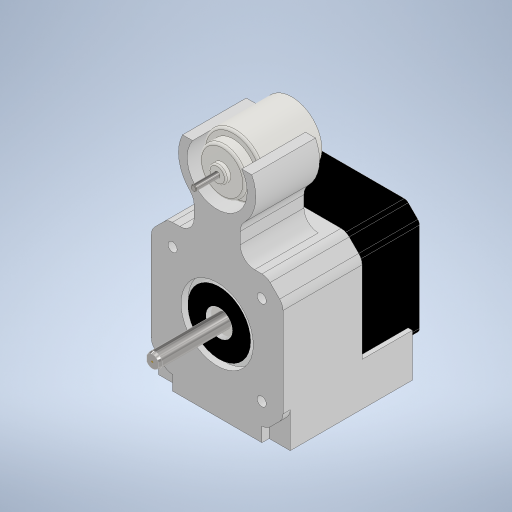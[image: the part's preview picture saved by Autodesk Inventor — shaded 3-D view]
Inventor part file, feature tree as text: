
AUTODESK INVENTOR PART (.ipt)
format: ipt  version: 2024.1 (Build 281209000, 209)  size: 689,664 bytes
history: native  units: mm
features: sketch x23, extrude x21, projected_geometry x11, fillet x10, other x5, chamfer x3
ambient origin geometry x8: Origin, YZ Plane, XZ Plane, XY Plane, X Axis, Y Axis, Z Axis, Center Point
bodies: Solid7 (feature_tree)
feature tree (73):
  other  "stepper"
  extrude  "Extrusion1"  Depth=41.8mm
  chamfer  "Chamfer1"  Distance=47.0mm
  fillet  "Fillet1"  Radius=2.0mm
  extrude  "Extrusion2"  Depth=41.8mm
  extrude  "Extrusion3"  Depth=20.9mm
  chamfer  "Chamfer2"  Distance=1.79mm
  other  "Work Point1"
  extrude  "Extrusion4"  Depth=5.0mm
  fillet  "Fillet2"  Radius=25.0mm
  extrude  "Extrusion5"  Depth=2.0mm
  extrude  "Extrusion6"  Depth=1.0mm
  extrude  "Extrusion7"  Depth=5.4mm
  extrude  "Extrusion8"  Depth=31.0mm
  extrude  "Extrusion9"  Depth=3.2mm
  extrude  "Extrusion16"  Depth=2.0mm
  fillet  "Fillet6"  Radius=2.5mm
  extrude  "Extrusion17"  Depth=42.5mm TaperAngle=0.0deg
  extrude  "Extrusion18"  Depth=5.0mm
  fillet  "Fillet7"  Radius=25.0mm
  fillet  "Fillet8"  Radius=20.9mm
  extrude  "Extrusion19"  Depth=45.8mm
  fillet  "Fillet9"  Radius=21.0mm
  extrude  "Extrusion20"  Depth=16.0mm
  fillet  "Fillet10"  Radius=3.8mm
  extrude  "Extrusion21"  Depth=6.05mm
  extrude  "Extrusion10"  Depth=2.0mm
  sketch  "Sketch11"  dims[d30=5.4mm d31=3.2mm]
  fillet  "Fillet3"  Radius=8.56mm
  extrude  "Extrusion11"  Depth=2.0mm
  fillet  "Fillet4"  Radius=18.75mm
  extrude  "Extrusion12"  Depth=5.0mm TaperAngle=45.0deg
  extrude  "Extrusion13"  Depth=33.35mm
  fillet  "Fillet5"  Radius=33.35mm
  extrude  "Extrusion14"  Depth=1.96mm
  extrude  "Extrusion15"  Depth=5.0mm
  chamfer  "Chamfer3"  Distance=6.03mm
  sketch  "Sketch17"  dims[d54=1.25mm d55=6.05mm]
  sketch  "Sketch1"  dims[d0=41.8mm d1=41.8mm d2=47.0mm d3=0.0mm]
  sketch  "Sketch2"  dims[d4=4.5mm d5=2.0mm d6=45.0deg d7=2.0mm]
  sketch  "Sketch3"  dims[d8=22.0mm d9=41.8mm]
  sketch  "Sketch4"  dims[d10=41.8mm d11=20.9mm]
  sketch  "Sketch5"  dims[d12=20.9mm d13=1.79mm d14=0.0mm]
  sketch  "Sketch6"  dims[d15=9.15mm d16=5.0mm d17=25.0mm d18=0.0mm]
  projected_geometry  "Projected Loop1"
  other  "casing"
  sketch  "Sketch7"  dims[d19=0.3mm d20=1.0mm d21=45.0deg d22=2.0mm]
  projected_geometry  "Projected Loop2"
  projected_geometry  "Projected Loop3"
  sketch  "Sketch8"  dims[d23=15.0mm d24=0.0mm d25=1.0mm]
  projected_geometry  "Projected Loop4"
  sketch  "Sketch9"  dims[d26=5.4mm d27=5.4mm]
  projected_geometry  "Projected Loop5"
  projected_geometry  "Projected Loop6"
  projected_geometry  "Projected Loop7"
  sketch  "Sketch10"  dims[d28=5.4mm d29=31.0mm]
  other  "genny"
  sketch  "Sketch12"  dims[d32=6.0mm d33=0.0mm d34=2.0mm d35=2.5mm d36=0.0mm]
  sketch  "Sketch13"  dims[d37=10.0mm d38=42.5mm d39=0.0mm]
  sketch  "Sketch14"  dims[d40=5.0mm d41=0.0mm d42=1.45mm d43=25.0mm d44=0.0mm d45=20.9mm]
  sketch  "Sketch15"  dims[d46=22.9mm d47=45.8mm d48=21.0mm d49=0.0mm]
  projected_geometry  "Projected Loop8"
  sketch  "Sketch16"  dims[d50=0.752mm d51=16.0mm d52=3.8mm d53=0.0mm]
  projected_geometry  "Projected Loop9"
  sketch  "Sketch18"  dims[d56=1.5mm d57=0.0mm d58=2.0mm d59=8.56mm d60=0.0mm]
  other  "generator"
  sketch  "Sketch19"  dims[d61=0.2mm d62=2.0mm d63=18.75mm d64=0.0mm]
  sketch  "Sketch20"  dims[d65=0.0mm d66=0.0mm d67=5.0mm d68=1.0mm d69=45.0deg]
  sketch  "Sketch21"  dims[d70=33.35mm d76=33.35mm d78=33.35mm]
  sketch  "Sketch22"  dims[d79=90.0mm d80=1.96mm]
  projected_geometry  "Projected Loop10"
  sketch  "Sketch23"  dims[d81=8.27mm d82=0.0mm d83=0.2mm d84=6.03mm d85=1.73mm d86=0.0mm d87=16.0mm d88=3.84mm d89=0.0mm d90=0.5mm d91=0.8mm d92=20.88mm d93=20.4mm d94=0.0mm d95=0.8mm d96=3.0mm d97=6.0mm d98=8.0mm d99=8.0mm d100=22.15mm d101=0.0mm d102=5.0mm d103=0.5mm d104=22.15mm d105=0.0mm]
  projected_geometry  "Projected Loop11"
